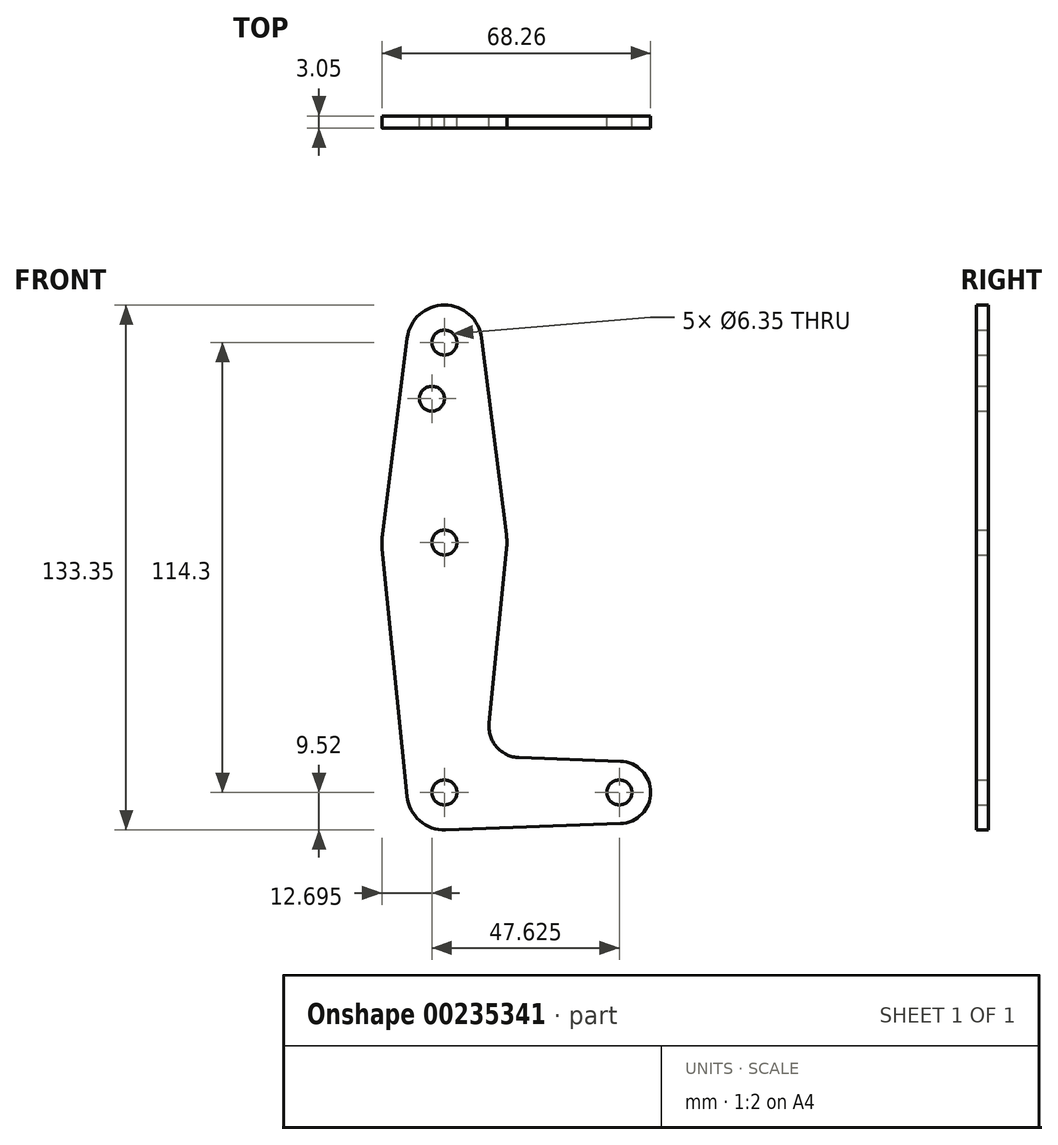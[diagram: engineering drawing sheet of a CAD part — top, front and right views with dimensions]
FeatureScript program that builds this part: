
annotation { "Feature Type Name" : "Feature", "Feature Type Description" : "" }
export const myFeature = defineFeature(function(context is Context, id is Id, definition is map)
    precondition{}
    {
        {
            var Q0;
            Q0=qCreatedBy(makeId("Front.planeOp"),FACE);
            var sketch = newSketch(context, id + "F0", { "sketchPlane" : qUnion([Q0])});
            skLineSegment(sketch, "E0", {"start": v(0, 0) * mm, "end": v(0, 114.3) * mm, "construction": true});
            skLineSegment(sketch, "E1", {"start": v(0, 0) * mm, "end": v(44.45, 0) * mm, "construction": true});
            skCircle(sketch, "E2", {"center": v(0, 0) * mm, "radius": 9.53 * mm});
            skCircle(sketch, "E3", {"center": v(0, 114.3) * mm, "radius": 9.53 * mm});
            skCircle(sketch, "E4", {"center": v(44.45, 0) * mm, "radius": 7.94 * mm});
            skCircle(sketch, "E5", {"center": v(0, 63.5) * mm, "radius": 15.88 * mm});
            skLineSegment(sketch, "E6", {"start": v(-9.45, 115.5) * mm, "end": v(-15.75, 65.48) * mm});
            skLineSegment(sketch, "E7", {"start": v(9.45, 115.5) * mm, "end": v(15.75, 65.48) * mm});
            skLineSegment(sketch, "E8", {"start": v(-15.8, 61.91) * mm, "end": v(-9.48, -0.95) * mm});
            skLineSegment(sketch, "E9", {"start": v(15.8, 61.91) * mm, "end": v(11.34, 17.6) * mm});
            skLineSegment(sketch, "E10", {"start": v(18.97, 8.85) * mm, "end": v(44.73, 7.93) * mm});
            skLineSegment(sketch, "E11", {"start": v(0.34, -9.52) * mm, "end": v(44.73, -7.93) * mm});
            skCircle(sketch, "E12", {"center": v(0, 114.3) * mm, "radius": 3.18 * mm});
            skCircle(sketch, "E13", {"center": v(0, 63.5) * mm, "radius": 3.18 * mm});
            skCircle(sketch, "E14", {"center": v(0, 0) * mm, "radius": 3.18 * mm});
            skCircle(sketch, "E15", {"center": v(44.45, 0) * mm, "radius": 3.18 * mm});
            skCircle(sketch, "E16", {"center": v(-3.18, 100.03) * mm, "radius": 3.18 * mm});
            skArc(sketch, "E17.filletArc", {"start": v(11.34, 17.6) * mm, "mid": v(13.26, 11.57) * mm, "end": v(18.97, 8.85) * mm});
            skSolve(sketch);
        }
        {
            var Q0;
            Q0 = qSketchRegion(id + "F0", true);
            extrude(context, id + "F1", {"entities" : qUnion([Q0]), "depth" : 3.05 * mm});
        }
    });
